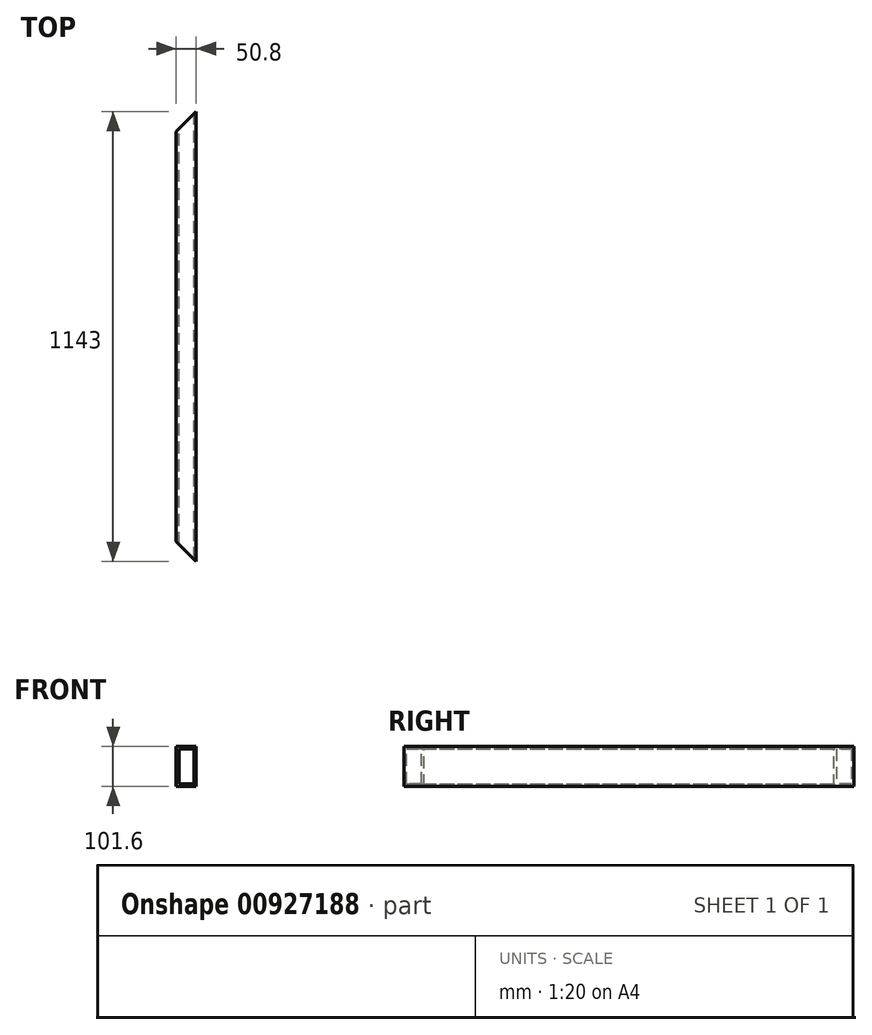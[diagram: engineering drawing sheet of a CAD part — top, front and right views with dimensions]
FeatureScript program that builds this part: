
annotation { "Feature Type Name" : "Feature", "Feature Type Description" : "" }
export const myFeature = defineFeature(function(context is Context, id is Id, definition is map)
    precondition{}
    {
        {
            var Q0;
            Q0=qCreatedBy(makeId("Front.planeOp"),FACE);
            var sketch = newSketch(context, id + "F0", { "sketchPlane" : qUnion([Q0])});
            skLineSegment(sketch, "E0.bottom", {"start": v(25.4, 50.8) * mm, "end": v(-25.4, 50.8) * mm});
            skLineSegment(sketch, "E0.top", {"start": v(25.4, -50.8) * mm, "end": v(-25.4, -50.8) * mm});
            skLineSegment(sketch, "E0.left", {"start": v(25.4, 50.8) * mm, "end": v(25.4, -50.8) * mm});
            skLineSegment(sketch, "E0.right", {"start": v(-25.4, 50.8) * mm, "end": v(-25.4, -50.8) * mm});
            skPoint(sketch, "E0.middle", {"position": v(0, 0) * mm});
            skLineSegment(sketch, "E1.0", {"start": v(19.05, 44.45) * mm, "end": v(-19.05, 44.45) * mm});
            skLineSegment(sketch, "E1.1", {"start": v(19.05, 44.45) * mm, "end": v(19.05, -44.45) * mm});
            skLineSegment(sketch, "E1.2", {"start": v(19.05, -44.45) * mm, "end": v(-19.05, -44.45) * mm});
            skLineSegment(sketch, "E1.3", {"start": v(-19.05, 44.45) * mm, "end": v(-19.05, -44.45) * mm});
            skSolve(sketch);
        }
        {
            var Q0;
            Q0 = qSketchRegion(id + "F0", true);
            extrude(context, id + "F1", {"entities" : qUnion([Q0]), "endBound" : BoundingType.SYMMETRIC, "depth" : 1143 * mm, "offsetDistance" : 25.4 * mm});
        }
        {
            var Q0;
            Q0=makeQuery(id+"F1.opExtrude","SWEPT_FACE",FACE,{"disambiguationData":[OSD([sQuery(id+"F0.wireOp",EDGE,"E0.bottom")])]});
            var sketch = newSketch(context, id + "F2", { "sketchPlane" : qUnion([Q0])});
            skLineSegment(sketch, "E2", {"start": v(25.4, -571.5) * mm, "end": v(-25.4, -520.7) * mm});
            skLineSegment(sketch, "E3", {"start": v(-25.4, -520.7) * mm, "end": v(-25.4, -571.5) * mm});
            skLineSegment(sketch, "E4", {"start": v(-25.4, -571.5) * mm, "end": v(25.4, -571.5) * mm});
            skLineSegment(sketch, "E5", {"start": v(-25.4, 571.5) * mm, "end": v(25.4, 571.5) * mm});
            skLineSegment(sketch, "E6", {"start": v(25.4, 571.5) * mm, "end": v(-25.4, 571.5) * mm});
            skLineSegment(sketch, "E7", {"start": v(-25.4, 520.7) * mm, "end": v(25.4, 571.5) * mm});
            skLineSegment(sketch, "E8", {"start": v(-25.4, 571.5) * mm, "end": v(-25.4, 520.7) * mm});
            skSolve(sketch);
        }
        {
            var Q0;
            Q0 = qSketchRegion(id + "F2", true);
            extrude(context, id + "F3", {"entities" : qUnion([Q0]), "operationType" : NewBodyOperationType.REMOVE, "endBound" : BoundingType.THROUGH_ALL, "oppositeDirection" : true, "depth" : 25.4 * mm, "offsetDistance" : 25.4 * mm});
        }
    });
